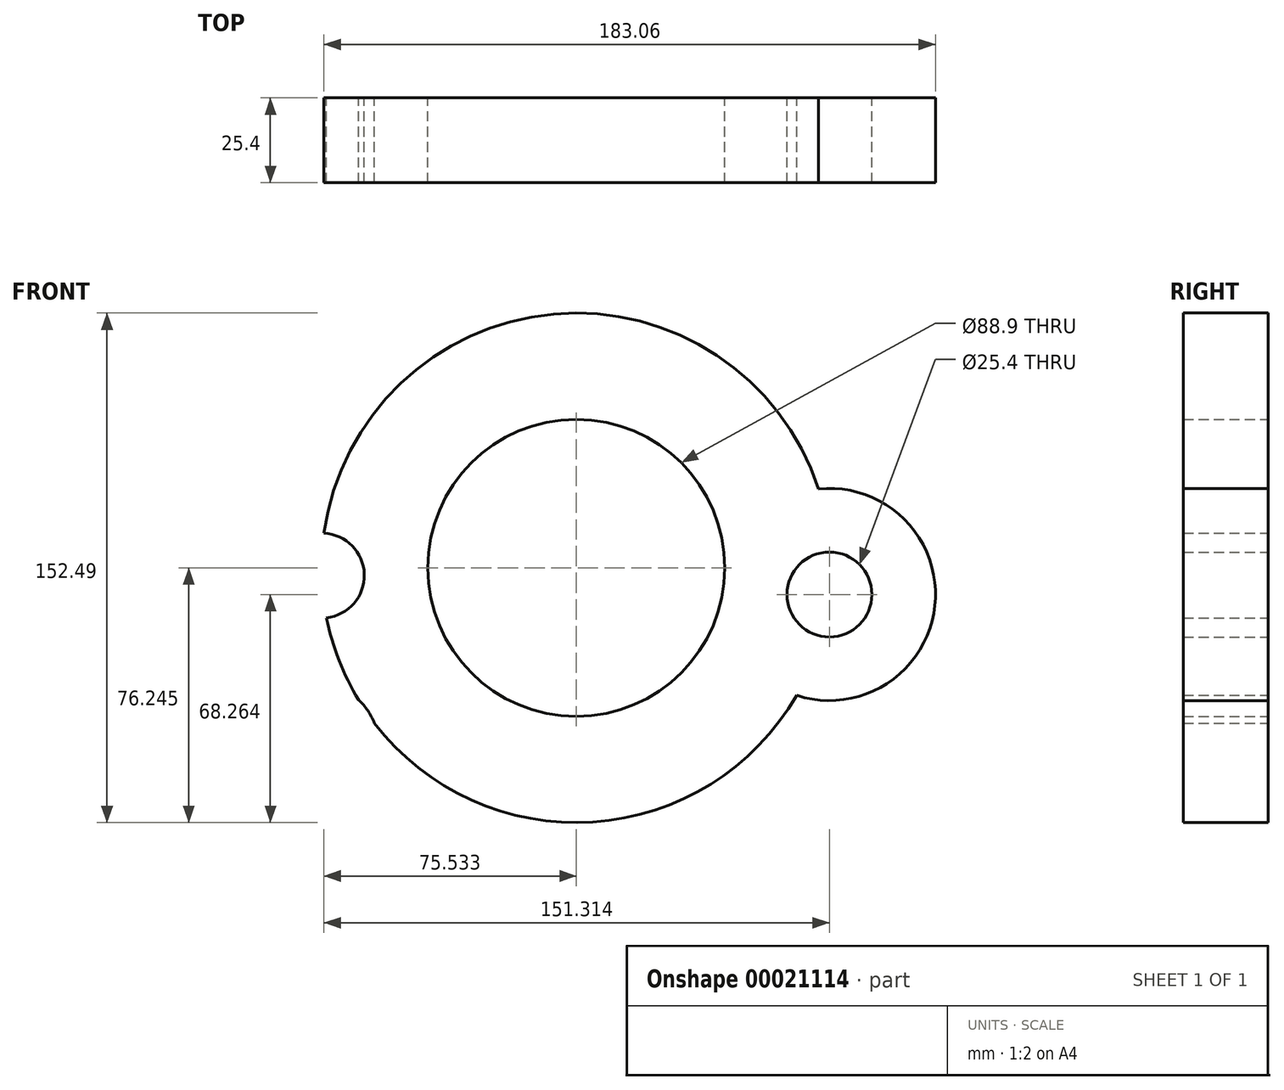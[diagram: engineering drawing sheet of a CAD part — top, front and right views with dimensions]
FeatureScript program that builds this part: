
annotation { "Feature Type Name" : "Feature", "Feature Type Description" : "" }
export const myFeature = defineFeature(function(context is Context, id is Id, definition is map)
    precondition{}
    {
        {
            var Q0;
            Q0=qCreatedBy(makeId("Front.planeOp"),FACE);
            var sketch = newSketch(context, id + "F0", { "sketchPlane" : qUnion([Q0])});
            skCircle(sketch, "E0", {"center": v(-181.16, 34.2) * mm, "radius": 12.7 * mm});
            skCircle(sketch, "E1", {"center": v(-29.22, 28.54) * mm, "radius": 12.7 * mm});
            skCircle(sketch, "E2", {"center": v(-105, 36.53) * mm, "radius": 44.45 * mm});
            skCircle(sketch, "E3", {"center": v(-29.22, 28.54) * mm, "radius": 31.75 * mm});
            skCircle(sketch, "E4", {"center": v(-181.16, 34.2) * mm, "radius": 31.75 * mm});
            skArc(sketch, "E5", {"start": v(-162.44, 59.84) * mm, "mid": v(-149.32, 61.17) * mm, "end": v(-137.45, 66.9) * mm});
            skArc(sketch, "E6", {"start": v(-71.52, 65.77) * mm, "mid": v(-58.92, 58.44) * mm, "end": v(-44.5, 56.38) * mm});
            skArc(sketch, "E7", {"start": v(-133.7, 2.59) * mm, "mid": v(-148.4, 8.2) * mm, "end": v(-164.13, 7.4) * mm});
            skArc(sketch, "E8", {"start": v(-48.44, 3.28) * mm, "mid": v(-64.22, 5.04) * mm, "end": v(-79.35, 0.22) * mm});
            skCircle(sketch, "E9", {"center": v(-105, 36.53) * mm, "radius": 76.24 * mm});
            skLineSegment(sketch, "E10", {"start": v(-105, 36.53) * mm, "end": v(-29.22, 28.54) * mm});
            skCircle(sketch, "E11", {"center": v(-187.25, 85.05) * mm, "radius": 19.05 * mm});
            skArc(sketch, "E12", {"start": v(-184.06, 65.81) * mm, "mid": v(-177.06, 68.87) * mm, "end": v(-171.4, 74) * mm});
            skArc(sketch, "E13", {"start": v(-36.1, 69.15) * mm, "mid": v(-29.66, 63.5) * mm, "end": v(-22.13, 59.42) * mm});
            skCircle(sketch, "E14", {"center": v(-183.14, -17) * mm, "radius": 19.05 * mm});
            skArc(sketch, "E15", {"start": v(-167.1, -7.7) * mm, "mid": v(-173.95, -0.42) * mm, "end": v(-183.64, 2.05) * mm});
            skArc(sketch, "E16", {"start": v(-26.2, -3.7) * mm, "mid": v(-36.89, -4.4) * mm, "end": v(-45.33, -11) * mm});
            skSolve(sketch);
        }
        {
            var Q0;
            {var subQ9=sQuery(id+"F0.wireOp",EDGE,"E7");Q0=makeQuery(id+"F0.imprint","IMPRINT",FACE,{"disambiguationData":[TD([[makeQuery(id+"F0.imprint","IMPRINT",EDGE,{"derivedFrom":subQ9}),1.0]])]});}
            var Q1;
            {var subQ5=sQuery(id+"F0.wireOp",EDGE,"E5");Q1=makeQuery(id+"F0.imprint","IMPRINT",FACE,{"disambiguationData":[TD([[makeQuery(id+"F0.imprint","IMPRINT",EDGE,{"derivedFrom":subQ5}),1.0]])]});}
            var Q2;
            {var subQ0=sQuery(id+"F0.wireOp",EDGE,"E9");var subQ1=sQuery(id+"F0.wireOp",EDGE,"E1");var subQ5=makeQuery(id+"F0.imprint","INTERSECT",VERTEX,{"disambiguationData":[OD(0.0)],"derivedFrom":[subQ1,subQ0]});Q2=makeQuery(id+"F0.imprint","IMPRINT",FACE,{"disambiguationData":[TD([[makeQuery(id+"F0.imprint","IMPRINT",EDGE,{"disambiguationData":[TD([[subQ5,1.0]])],"derivedFrom":subQ1}),-1.0]])]});}
            var Q3;
            {var subQ0=sQuery(id+"F0.wireOp",EDGE,"E10");var subQ3=sQuery(id+"F0.wireOp",EDGE,"E1");var subQ4=makeQuery(id+"F0.imprint","INTERSECT",VERTEX,{"derivedFrom":[subQ3,subQ0]});Q3=makeQuery(id+"F0.imprint","IMPRINT",FACE,{"disambiguationData":[TD([[makeQuery(id+"F0.imprint","IMPRINT",EDGE,{"disambiguationData":[TD([[subQ4,1.0]])],"derivedFrom":subQ3}),-1.0]])]});}
            var Q4;
            {var subQ0=sQuery(id+"F0.wireOp",EDGE,"E6");Q4=makeQuery(id+"F0.imprint","IMPRINT",FACE,{"disambiguationData":[TD([[makeQuery(id+"F0.imprint","IMPRINT",EDGE,{"derivedFrom":subQ0}),-1.0]])]});}
            var Q5;
            {var subQ0=sQuery(id+"F0.wireOp",EDGE,"E10");var subQ3=sQuery(id+"F0.wireOp",EDGE,"E1");var subQ4=makeQuery(id+"F0.imprint","INTERSECT",VERTEX,{"derivedFrom":[subQ3,subQ0]});Q5=makeQuery(id+"F0.imprint","IMPRINT",FACE,{"disambiguationData":[TD([[makeQuery(id+"F0.imprint","IMPRINT",EDGE,{"disambiguationData":[TD([[subQ4,-1.0]])],"derivedFrom":subQ3}),-1.0]])]});}
            var Q6;
            {var subQ0=sQuery(id+"F0.wireOp",EDGE,"E8");Q6=makeQuery(id+"F0.imprint","IMPRINT",FACE,{"disambiguationData":[TD([[makeQuery(id+"F0.imprint","IMPRINT",EDGE,{"derivedFrom":subQ0}),-1.0]])]});}
            var Q7;
            {var subQ0=sQuery(id+"F0.wireOp",EDGE,"E5");Q7=makeQuery(id+"F0.imprint","IMPRINT",FACE,{"disambiguationData":[TD([[makeQuery(id+"F0.imprint","IMPRINT",EDGE,{"derivedFrom":subQ0}),-1.0]])]});}
            var Q8;
            {var subQ0=sQuery(id+"F0.wireOp",EDGE,"E7");Q8=makeQuery(id+"F0.imprint","IMPRINT",FACE,{"disambiguationData":[TD([[makeQuery(id+"F0.imprint","IMPRINT",EDGE,{"derivedFrom":subQ0}),-1.0]])]});}
            var Q9;
            {var subQ0=sQuery(id+"F0.wireOp",EDGE,"E9");var subQ1=sQuery(id+"F0.wireOp",EDGE,"E0");var subQ6=makeQuery(id+"F0.imprint","INTERSECT",VERTEX,{"disambiguationData":[OD(0.0)],"derivedFrom":[subQ1,subQ0]});Q9=makeQuery(id+"F0.imprint","IMPRINT",FACE,{"disambiguationData":[TD([[makeQuery(id+"F0.imprint","IMPRINT",EDGE,{"disambiguationData":[TD([[subQ6,1.0]])],"derivedFrom":subQ1}),-1.0]])]});}
            extrude(context, id + "F1", {"entities" : qUnion([Q0, Q1, Q2, Q3, Q4, Q5, Q6, Q7, Q8, Q9]), "depth" : 25.4 * mm});
        }
        {
            var Q0;
            Q0=sQuery(id+"F0.wireOp",EDGE,"E13");
            var Q1;
            Q1=sQuery(id+"F0.wireOp",EDGE,"E4");
            extrude(context, id + "F2", {"bodyType" : ToolBodyType.SURFACE, "surfaceEntities" : qUnion([Q0, Q1]), "depth" : 25.4 * mm});
        }
        {
            var Q0;
            Q0=sQuery(id+"F0.wireOp",EDGE,"E13");
            var Q1;
            Q1=sQuery(id+"F0.wireOp",EDGE,"E4");
            extrude(context, id + "F3", {"bodyType" : ToolBodyType.SURFACE, "surfaceEntities" : qUnion([Q0, Q1]), "depth" : 25.4 * mm});
        }
        {
            var Q0;
            Q0=sQuery(id+"F0.wireOp",EDGE,"E16");
            var Q1;
            Q1=sQuery(id+"F0.wireOp",EDGE,"E15");
            var Q2;
            Q2=sQuery(id+"F0.wireOp",EDGE,"E4");
            extrude(context, id + "F4", {"bodyType" : ToolBodyType.SURFACE, "surfaceEntities" : qUnion([Q0, Q1, Q2]), "depth" : 25.4 * mm});
        }
    });
